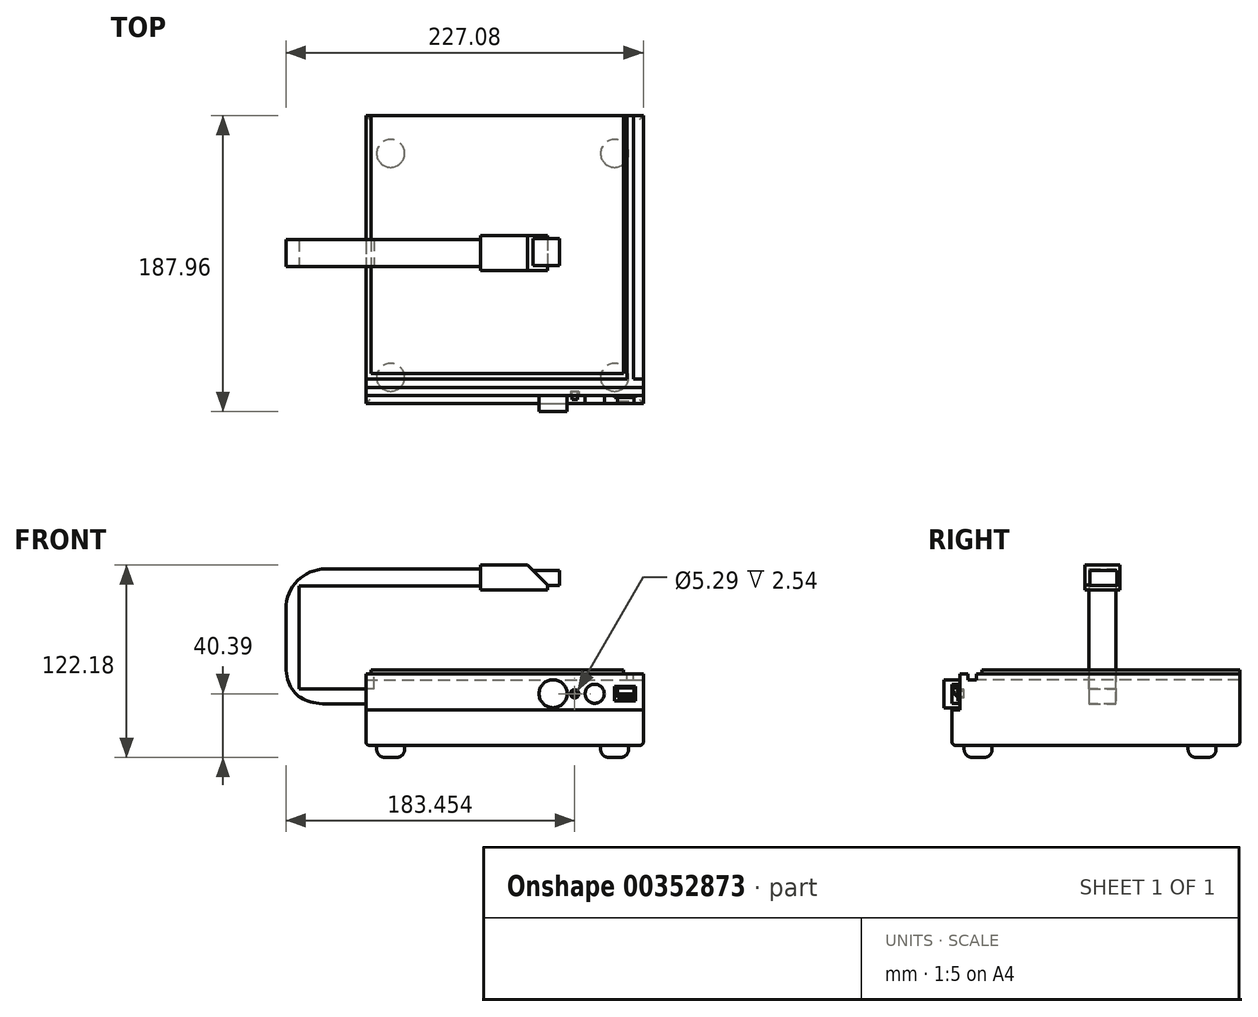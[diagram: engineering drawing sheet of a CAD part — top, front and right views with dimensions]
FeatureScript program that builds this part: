
annotation { "Feature Type Name" : "Feature", "Feature Type Description" : "" }
export const myFeature = defineFeature(function(context is Context, id is Id, definition is map)
    precondition{}
    {
        {
            var Q0;
            Q0=qCreatedBy(makeId("Front.planeOp"),FACE);
            var sketch = newSketch(context, id + "F0", { "sketchPlane" : qUnion([Q0])});
            skLineSegment(sketch, "E0.bottom", {"start": v(-86.87, 37.85) * mm, "end": v(89.4, 37.85) * mm});
            skLineSegment(sketch, "E0.top", {"start": v(-86.87, -32.77) * mm, "end": v(89.4, -32.77) * mm});
            skLineSegment(sketch, "E0.left", {"start": v(-86.87, 37.85) * mm, "end": v(-86.87, -32.77) * mm});
            skLineSegment(sketch, "E0.right", {"start": v(89.4, 37.85) * mm, "end": v(89.4, -32.77) * mm});
            skSolve(sketch);
        }
        {
            var Q0;
            Q0=makeQuery(id+"F0.imprint","IMPRINT",FACE,{"disambiguationData":[TD([[makeQuery(id+"F0.imprint","IMPRINT",EDGE,{"derivedFrom":sQuery(id+"F0.wireOp",EDGE,"E0.bottom")}),-1.0]])]});
            extrude(context, id + "F1", {"entities" : qUnion([Q0]), "depth" : 177.8 * mm});
        }
        {
            var Q0;
            Q0=makeQuery(id+"F1.opExtrude","SWEPT_FACE",FACE,{"disambiguationData":[OSD([sQuery(id+"F0.wireOp",EDGE,"E0.bottom")])]});
            extrude(context, id + "F2", {"entities" : qUnion([Q0]), "operationType" : NewBodyOperationType.REMOVE, "oppositeDirection" : true, "depth" : 25.4 * mm});
        }
        {
            var Q0;
            Q0=makeQuery(id+"F1.opExtrude","CAP_FACE",FACE,{"disambiguationData":[OSD([sQuery(id+"F0.wireOp",EDGE,"E0.bottom"),sQuery(id+"F0.wireOp",EDGE,"E0.top"),sQuery(id+"F0.wireOp",EDGE,"E0.left"),sQuery(id+"F0.wireOp",EDGE,"E0.right")])],"isStart":false});
            var sketch = newSketch(context, id + "F3", { "sketchPlane" : qUnion([Q0])});
            skLineSegment(sketch, "E1", {"start": v(-86.87, -10.16) * mm, "end": v(89.4, -10.16) * mm});
            skLineSegment(sketch, "E2", {"start": v(-86.87, -4.75) * mm, "end": v(89.4, -4.75) * mm});
            skSolve(sketch);
        }
        {
            var Q0;
            Q0 = qSketchRegion(id + "F3", true);
            var Q1;
            {var subQ0=sQuery(id+"F3.wireOp",EDGE,"E1");Q1=makeQuery(id+"F3.imprint","IMPRINT",FACE,{"disambiguationData":[TD([[makeQuery(id+"F3.imprint","IMPRINT",EDGE,{"derivedFrom":subQ0}),-1.0]])]});}
            extrude(context, id + "F4", {"entities" : qUnion([Q0, Q1]), "operationType" : NewBodyOperationType.ADD, "depth" : 5.08 * mm});
        }
        {
            var Q0;
            {var subQ0=sQuery(id+"F0.wireOp",EDGE,"E0.left");Q0=makeQuery(id+"F4.boolean.opBoolean","MERGE",FACE,{"derivedFrom":[makeQuery(id+"F1.opExtrude","SWEPT_FACE",FACE,{"disambiguationData":[OSD([subQ0])]}),makeQuery(id+"F4.opExtrude","SWEPT_FACE",FACE,{"disambiguationData":[OSD([subQ0])]})]});}
            var sketch = newSketch(context, id + "F5", { "sketchPlane" : qUnion([Q0])});
            skLineSegment(sketch, "E3.bottom", {"start": v(78.74, 12.45) * mm, "end": v(96.01, 12.45) * mm});
            skLineSegment(sketch, "E3.top", {"start": v(78.74, -6.35) * mm, "end": v(96.01, -6.35) * mm});
            skLineSegment(sketch, "E3.left", {"start": v(78.74, 12.45) * mm, "end": v(78.74, -6.35) * mm});
            skLineSegment(sketch, "E3.right", {"start": v(96.01, 12.45) * mm, "end": v(96.01, -6.35) * mm});
            skLineSegment(sketch, "E4", {"start": v(78.74, 3.05) * mm, "end": v(96.01, 3.05) * mm});
            skSolve(sketch);
        }
        {
            var Q0;
            {var subQ0=sQuery(id+"F5.wireOp",EDGE,"E3.top");Q0=makeQuery(id+"F5.imprint","IMPRINT",FACE,{"disambiguationData":[TD([[makeQuery(id+"F5.imprint","IMPRINT",EDGE,{"derivedFrom":subQ0}),1.0]])]});}
            extrude(context, id + "F6", {"entities" : qUnion([Q0]), "operationType" : NewBodyOperationType.ADD, "depth" : 50.8 * mm});
        }
        {
            var Q0;
            Q0=makeQuery(id+"F6.opExtrude","SWEPT_FACE",FACE,{"disambiguationData":[OSD([sQuery(id+"F5.wireOp",EDGE,"E4")])]});
            var sketch = newSketch(context, id + "F7", { "sketchPlane" : qUnion([Q0])});
            skLineSegment(sketch, "E5", {"start": v(-129.22, -96.01) * mm, "end": v(-129.22, -78.74) * mm});
            skSolve(sketch);
        }
        {
            var Q0;
            Q0 = qSketchRegion(id + "F7", true);
            var Q1;
            {var subQ0=sQuery(id+"F7.wireOp",EDGE,"E5");Q1=makeQuery(id+"F7.imprint","IMPRINT",FACE,{"disambiguationData":[TD([[makeQuery(id+"F7.imprint","IMPRINT",EDGE,{"derivedFrom":subQ0}),1.0]])]});}
            extrude(context, id + "F8", {"entities" : qUnion([Q0, Q1]), "operationType" : NewBodyOperationType.ADD, "depth" : 76.2 * mm});
        }
        {
            var Q0;
            Q0=makeQuery(id+"F8.opExtrude","SWEPT_FACE",FACE,{"disambiguationData":[OSD([sQuery(id+"F7.wireOp",EDGE,"E5")])]});
            var sketch = newSketch(context, id + "F9", { "sketchPlane" : qUnion([Q0])});
            skLineSegment(sketch, "E6", {"start": v(-78.74, 68.6) * mm, "end": v(-96.01, 68.6) * mm});
            skSolve(sketch);
        }
        {
            var Q0;
            Q0 = qSketchRegion(id + "F9", true);
            var Q1;
            {var subQ0=sQuery(id+"F9.wireOp",EDGE,"E6");Q1=makeQuery(id+"F9.imprint","IMPRINT",FACE,{"disambiguationData":[TD([[makeQuery(id+"F9.imprint","IMPRINT",EDGE,{"derivedFrom":subQ0}),-1.0]])]});}
            extrude(context, id + "F10", {"entities" : qUnion([Q0, Q1]), "operationType" : NewBodyOperationType.ADD, "depth" : 157.73 * mm});
        }
        {
            var Q0;
            Q0=makeQuery(id+"F10.opExtrude","CAP_EDGE",EDGE,{"disambiguationData":[OSD([sQuery(id+"F9.wireOp",EDGE,"E6")])],"isStart":true});
            var Q1;
            Q1=makeQuery(id+"F8.opExtrude","CAP_EDGE",EDGE,{"disambiguationData":[OSD([sQuery(id+"F5.wireOp",EDGE,"E4")])],"isStart":false});
            fillet(context, id + "F11", {"entities" : qUnion([Q0, Q1]), "radius" : 25.4 * mm, "tangentPropagation" : true, "allowEdgeOverflow" : false});
        }
        {
            var Q0;
            Q0=makeQuery(id+"F8.opExtrude","CAP_EDGE",EDGE,{"disambiguationData":[OSD([sQuery(id+"F7.wireOp",EDGE,"E5")])],"isStart":true});
            var Q1;
            Q1=makeQuery(id+"F6.opExtrude","CAP_EDGE",EDGE,{"disambiguationData":[OSD([sQuery(id+"F5.wireOp",EDGE,"E3.top")])],"isStart":false});
            fillet(context, id + "F12", {"entities" : qUnion([Q0, Q1]), "radius" : 25.4 * mm, "tangentPropagation" : true, "rho" : 0.5, "crossSection" : FilletCrossSection.CONIC, "allowEdgeOverflow" : false});
        }
        {
            var Q0;
            Q0=makeQuery(id+"F1.opExtrude","CAP_FACE",FACE,{"disambiguationData":[OSD([sQuery(id+"F0.wireOp",EDGE,"E0.bottom"),sQuery(id+"F0.wireOp",EDGE,"E0.top"),sQuery(id+"F0.wireOp",EDGE,"E0.left"),sQuery(id+"F0.wireOp",EDGE,"E0.right")])],"isStart":false});
            var sketch = newSketch(context, id + "F13", { "sketchPlane" : qUnion([Q0])});
            skCircle(sketch, "E7", {"center": v(58.46, 0) * mm, "radius": 6.08 * mm});
            skSolve(sketch);
        }
        {
            var Q0;
            Q0 = qSketchRegion(id + "F13", true);
            extrude(context, id + "F14", {"entities" : qUnion([Q0]), "operationType" : NewBodyOperationType.ADD, "depth" : 5.08 * mm});
        }
        {
            var Q0;
            Q0=makeQuery(id+"F1.opExtrude","CAP_FACE",FACE,{"disambiguationData":[OSD([sQuery(id+"F0.wireOp",EDGE,"E0.bottom"),sQuery(id+"F0.wireOp",EDGE,"E0.top"),sQuery(id+"F0.wireOp",EDGE,"E0.left"),sQuery(id+"F0.wireOp",EDGE,"E0.right")])],"isStart":false});
            var sketch = newSketch(context, id + "F15", { "sketchPlane" : qUnion([Q0])});
            skCircle(sketch, "E8", {"center": v(32.04, 0) * mm, "radius": 8.9 * mm});
            skSolve(sketch);
        }
        {
            var Q0;
            Q0 = qSketchRegion(id + "F15", true);
            extrude(context, id + "F16", {"entities" : qUnion([Q0]), "operationType" : NewBodyOperationType.ADD, "depth" : 10.16 * mm});
        }
        {
            var Q0;
            Q0=makeQuery(id+"F2.boolean.opBoolean","COPY",FACE,{"derivedFrom":makeQuery(id+"F2.opExtrude","CAP_FACE",FACE,{"disambiguationData":[OSD([sQuery(id+"F0.wireOp",EDGE,"E0.bottom")])],"isStart":false})});
            var sketch = newSketch(context, id + "F17", { "sketchPlane" : qUnion([Q0])});
            skLineSegment(sketch, "E9.bottom", {"start": v(-83.65, 0) * mm, "end": v(76.74, 0) * mm});
            skLineSegment(sketch, "E9.top", {"start": v(-83.65, -163.84) * mm, "end": v(76.74, -163.84) * mm});
            skLineSegment(sketch, "E9.left", {"start": v(-83.65, 0) * mm, "end": v(-83.65, -163.84) * mm});
            skLineSegment(sketch, "E9.right", {"start": v(76.74, 0) * mm, "end": v(76.74, -163.84) * mm});
            skSolve(sketch);
        }
        {
            var Q0;
            Q0 = qSketchRegion(id + "F17", true);
            extrude(context, id + "F18", {"entities" : qUnion([Q0]), "operationType" : NewBodyOperationType.ADD, "depth" : 2.54 * mm});
        }
        {
            var Q0;
            {var subQ0=sQuery(id+"F0.wireOp",EDGE,"E0.left");Q0=makeQuery(id+"F4.boolean.opBoolean","MERGE",FACE,{"derivedFrom":[makeQuery(id+"F1.opExtrude","SWEPT_FACE",FACE,{"disambiguationData":[OSD([subQ0])]}),makeQuery(id+"F4.opExtrude","SWEPT_FACE",FACE,{"disambiguationData":[OSD([subQ0])]})]});}
            var sketch = newSketch(context, id + "F19", { "sketchPlane" : qUnion([Q0])});
            skLineSegment(sketch, "E10.bottom", {"start": v(96.01, 3.05) * mm, "end": v(78.68, 3.05) * mm});
            skLineSegment(sketch, "E10.top", {"start": v(96.01, 12.45) * mm, "end": v(78.68, 12.45) * mm});
            skLineSegment(sketch, "E10.left", {"start": v(96.01, 3.05) * mm, "end": v(96.01, 12.45) * mm});
            skLineSegment(sketch, "E10.right", {"start": v(78.68, 3.05) * mm, "end": v(78.68, 12.45) * mm});
            skSolve(sketch);
        }
        {
            var Q0;
            Q0 = qSketchRegion(id + "F19", true);
            extrude(context, id + "F20", {"entities" : qUnion([Q0]), "operationType" : NewBodyOperationType.REMOVE, "oppositeDirection" : true, "depth" : 5.08 * mm});
        }
        {
            var Q0;
            {var subQ1=sQuery(id+"F0.wireOp",EDGE,"E0.right");var subQ3=sQuery(id+"F0.wireOp",EDGE,"E0.bottom");Q0=makeQuery(id+"F20.boolean.opBoolean","SPLIT",FACE,{"disambiguationData":[TD([makeQuery(id+"F1.opExtrude","SWEPT_FACE",FACE,{"disambiguationData":[OSD([subQ1])]})])],"derivedFrom":makeQuery(id+"F2.boolean.opBoolean","COPY",FACE,{"derivedFrom":makeQuery(id+"F2.opExtrude","CAP_FACE",FACE,{"disambiguationData":[OSD([subQ3])],"isStart":false})})});}
            var sketch = newSketch(context, id + "F21", { "sketchPlane" : qUnion([Q0])});
            skLineSegment(sketch, "E11.bottom", {"start": v(-86.87, -167.28) * mm, "end": v(89.4, -167.28) * mm});
            skLineSegment(sketch, "E11.top", {"start": v(-86.87, -172.6) * mm, "end": v(89.4, -172.6) * mm});
            skLineSegment(sketch, "E11.left", {"start": v(-86.87, -167.28) * mm, "end": v(-86.87, -172.6) * mm});
            skLineSegment(sketch, "E11.right", {"start": v(89.4, -167.28) * mm, "end": v(89.4, -172.6) * mm});
            skPoint(sketch, "E12.oppositeSnap0", {"position": v(83.07, 0) * mm});
            skLineSegment(sketch, "E12.bottom", {"start": v(78.93, 0) * mm, "end": v(83.07, 0) * mm});
            skLineSegment(sketch, "E12.top", {"start": v(78.93, -167.28) * mm, "end": v(83.07, -167.28) * mm});
            skLineSegment(sketch, "E12.left", {"start": v(78.93, 0) * mm, "end": v(78.93, -167.28) * mm});
            skLineSegment(sketch, "E12.right", {"start": v(83.07, 0) * mm, "end": v(83.07, -167.28) * mm});
            skSolve(sketch);
        }
        {
            var Q0;
            Q0 = qSketchRegion(id + "F21", true);
            extrude(context, id + "F22", {"entities" : qUnion([Q0]), "operationType" : NewBodyOperationType.REMOVE, "oppositeDirection" : true, "depth" : 3.8 * mm});
        }
        {
            var Q0;
            Q0=makeQuery(id+"F1.opExtrude","CAP_FACE",FACE,{"disambiguationData":[OSD([sQuery(id+"F0.wireOp",EDGE,"E0.bottom"),sQuery(id+"F0.wireOp",EDGE,"E0.top"),sQuery(id+"F0.wireOp",EDGE,"E0.left"),sQuery(id+"F0.wireOp",EDGE,"E0.right")])],"isStart":false});
            var sketch = newSketch(context, id + "F23", { "sketchPlane" : qUnion([Q0])});
            skLineSegment(sketch, "E13.bottom", {"start": v(71.1, 4.67) * mm, "end": v(84.47, 4.67) * mm});
            skLineSegment(sketch, "E13.top", {"start": v(71.1, -4.5) * mm, "end": v(84.47, -4.5) * mm});
            skLineSegment(sketch, "E13.left", {"start": v(71.1, 4.67) * mm, "end": v(71.1, -4.5) * mm});
            skLineSegment(sketch, "E13.right", {"start": v(84.47, 4.67) * mm, "end": v(84.47, -4.5) * mm});
            skSolve(sketch);
        }
        {
            var Q0;
            Q0 = qSketchRegion(id + "F23", true);
            extrude(context, id + "F24", {"entities" : qUnion([Q0]), "operationType" : NewBodyOperationType.ADD, "depth" : 1.27 * mm});
        }
        {
            var Q0;
            {var subQ0=sQuery(id+"F0.wireOp",EDGE,"E0.top");Q0=makeQuery(id+"F4.boolean.opBoolean","MERGE",FACE,{"derivedFrom":[makeQuery(id+"F1.opExtrude","SWEPT_FACE",FACE,{"disambiguationData":[OSD([subQ0])]}),makeQuery(id+"F4.opExtrude","SWEPT_FACE",FACE,{"disambiguationData":[OSD([subQ0])]})]});}
            fillet(context, id + "F25", {"entities" : qUnion([Q0]), "radius" : 2.54 * mm, "tangentPropagation" : true, "rho" : 0.5, "crossSection" : FilletCrossSection.CONIC, "allowEdgeOverflow" : false});
        }
        {
            var Q0;
            Q0=makeQuery(id+"F24.opExtrude","CAP_FACE",FACE,{"disambiguationData":[OSD([sQuery(id+"F23.wireOp",EDGE,"E13.bottom"),sQuery(id+"F23.wireOp",EDGE,"E13.top"),sQuery(id+"F23.wireOp",EDGE,"E13.left"),sQuery(id+"F23.wireOp",EDGE,"E13.right")])],"isStart":false});
            var sketch = newSketch(context, id + "F26", { "sketchPlane" : qUnion([Q0])});
            skLineSegment(sketch, "E14.bottom", {"start": v(83.37, 3.58) * mm, "end": v(72.82, 3.58) * mm});
            skLineSegment(sketch, "E14.top", {"start": v(83.37, -3.58) * mm, "end": v(72.82, -3.58) * mm});
            skLineSegment(sketch, "E14.left", {"start": v(83.37, 3.58) * mm, "end": v(83.37, -3.58) * mm});
            skLineSegment(sketch, "E14.right", {"start": v(72.82, 3.58) * mm, "end": v(72.82, -3.58) * mm});
            skPoint(sketch, "E14.middle", {"position": v(78.1, 0) * mm});
            skSolve(sketch);
        }
        {
            var Q0;
            Q0=makeQuery(id+"F26.imprint","IMPRINT",FACE,{"disambiguationData":[TD([[makeQuery(id+"F26.imprint","IMPRINT",EDGE,{"derivedFrom":sQuery(id+"F26.wireOp",EDGE,"E14.bottom")}),1.0]])]});
            extrude(context, id + "F27", {"entities" : qUnion([Q0]), "operationType" : NewBodyOperationType.ADD, "depth" : 3.8 * mm});
        }
        {
            var Q0;
            Q0=makeQuery(id+"F27.opExtrude","CAP_EDGE",EDGE,{"disambiguationData":[OSD([sQuery(id+"F26.wireOp",EDGE,"E14.top")])],"isStart":false});
            chamfer(context, id + "F28", {"entities" : qUnion([Q0]), "width" : 5.08 * mm, "tangentPropagation" : true});
        }
        {
            var Q0;
            {var subQ0=sQuery(id+"F26.wireOp",EDGE,"E14.top");Q0=makeQuery(id+"F28.opChamfer","BLEND_EDGE",EDGE,{"blendedFrom":[makeQuery(id+"F27.opExtrude","CAP_EDGE",EDGE,{"disambiguationData":[OSD([subQ0])],"isStart":false}),makeQuery(id+"F27.opExtrude","CAP_FACE",FACE,{"disambiguationData":[OSD([sQuery(id+"F26.wireOp",EDGE,"E14.bottom"),subQ0,sQuery(id+"F26.wireOp",EDGE,"E14.left"),sQuery(id+"F26.wireOp",EDGE,"E14.right")])],"isStart":false})],"blendedInto":[makeQuery(id+"F27.opExtrude","CAP_FACE",FACE,{"disambiguationData":[OSD([sQuery(id+"F26.wireOp",EDGE,"E14.bottom"),subQ0,sQuery(id+"F26.wireOp",EDGE,"E14.left"),sQuery(id+"F26.wireOp",EDGE,"E14.right")])],"isStart":false})]});}
            chamfer(context, id + "F29", {"entities" : qUnion([Q0]), "width" : 5.08 * mm, "tangentPropagation" : true});
        }
        {
            var Q0;
            Q0=makeQuery(id+"F1.opExtrude","CAP_FACE",FACE,{"disambiguationData":[OSD([sQuery(id+"F0.wireOp",EDGE,"E0.bottom"),sQuery(id+"F0.wireOp",EDGE,"E0.top"),sQuery(id+"F0.wireOp",EDGE,"E0.left"),sQuery(id+"F0.wireOp",EDGE,"E0.right")])],"isStart":false});
            var sketch = newSketch(context, id + "F30", { "sketchPlane" : qUnion([Q0])});
            skCircle(sketch, "E15", {"center": v(45.78, 0) * mm, "radius": 2.64 * mm});
            skSolve(sketch);
        }
        {
            var Q0;
            Q0=makeQuery(id+"F30.imprint","IMPRINT",FACE,{"disambiguationData":[TD([[makeQuery(id+"F30.imprint","IMPRINT",EDGE,{"derivedFrom":sQuery(id+"F30.wireOp",EDGE,"E15")}),1.0]])]});
            extrude(context, id + "F31", {"entities" : qUnion([Q0]), "operationType" : NewBodyOperationType.REMOVE, "oppositeDirection" : true, "depth" : 2.54 * mm});
        }
        {
            var Q0;
            Q0=makeQuery(id+"F31.boolean.opBoolean","COPY",FACE,{"derivedFrom":makeQuery(id+"F31.opExtrude","CAP_FACE",FACE,{"disambiguationData":[OSD([sQuery(id+"F30.wireOp",EDGE,"E15")])],"isStart":false})});
            var sketch = newSketch(context, id + "F32", { "sketchPlane" : qUnion([Q0])});
            skCircle(sketch, "E16", {"center": v(45.78, 0) * mm, "radius": 1.76 * mm});
            skSolve(sketch);
        }
        {
            var Q0;
            Q0 = qSketchRegion(id + "F32", true);
            extrude(context, id + "F33", {"entities" : qUnion([Q0]), "operationType" : NewBodyOperationType.ADD, "depth" : 5.08 * mm});
        }
        {
            var Q0;
            {var subQ0=sQuery(id+"F0.wireOp",EDGE,"E0.top");Q0=makeQuery(id+"F4.boolean.opBoolean","MERGE",FACE,{"derivedFrom":[makeQuery(id+"F1.opExtrude","SWEPT_FACE",FACE,{"disambiguationData":[OSD([subQ0])]}),makeQuery(id+"F4.opExtrude","SWEPT_FACE",FACE,{"disambiguationData":[OSD([subQ0])]})]});}
            var sketch = newSketch(context, id + "F34", { "sketchPlane" : qUnion([Q0])});
            skLineSegment(sketch, "E17.bottom", {"start": v(71.12, 166.26) * mm, "end": v(-71.12, 166.26) * mm});
            skLineSegment(sketch, "E17.top", {"start": v(71.12, 24.02) * mm, "end": v(-71.12, 24.02) * mm});
            skLineSegment(sketch, "E17.left", {"start": v(71.12, 166.26) * mm, "end": v(71.12, 24.02) * mm});
            skLineSegment(sketch, "E17.right", {"start": v(-71.12, 166.26) * mm, "end": v(-71.12, 24.02) * mm});
            skPoint(sketch, "E17.middle", {"position": v(0, 95.14) * mm});
            skCircle(sketch, "E18", {"center": v(-71.12, 166.26) * mm, "radius": 8.9 * mm});
            skCircle(sketch, "E19", {"center": v(71.12, 166.26) * mm, "radius": 8.9 * mm});
            skCircle(sketch, "E20", {"center": v(71.12, 24.02) * mm, "radius": 8.9 * mm});
            skCircle(sketch, "E21", {"center": v(-71.12, 24.02) * mm, "radius": 8.9 * mm});
            skSolve(sketch);
        }
        {
            var Q0;
            {var subQ0=sQuery(id+"F34.wireOp",EDGE,"E17.right");var subQ1=sQuery(id+"F34.wireOp",EDGE,"E17.bottom");var subQ2=makeQuery(id+"F34.imprint","INTERSECT",VERTEX,{"derivedFrom":[subQ1,subQ0]});Q0=makeQuery(id+"F34.imprint","IMPRINT",FACE,{"disambiguationData":[TD([[makeQuery(id+"F34.imprint","IMPRINT",EDGE,{"disambiguationData":[TD([[subQ2,1.0]])],"derivedFrom":subQ1}),1.0]])]});}
            var Q1;
            {var subQ0=sQuery(id+"F34.wireOp",EDGE,"E17.right");var subQ1=sQuery(id+"F34.wireOp",EDGE,"E17.bottom");var subQ2=makeQuery(id+"F34.imprint","INTERSECT",VERTEX,{"derivedFrom":[subQ1,subQ0]});Q1=makeQuery(id+"F34.imprint","IMPRINT",FACE,{"disambiguationData":[TD([[makeQuery(id+"F34.imprint","IMPRINT",EDGE,{"disambiguationData":[TD([[subQ2,1.0]])],"derivedFrom":subQ1}),-1.0]])]});}
            var Q2;
            {var subQ0=sQuery(id+"F34.wireOp",EDGE,"E17.left");var subQ1=sQuery(id+"F34.wireOp",EDGE,"E17.bottom");var subQ2=makeQuery(id+"F34.imprint","INTERSECT",VERTEX,{"derivedFrom":[subQ1,subQ0]});Q2=makeQuery(id+"F34.imprint","IMPRINT",FACE,{"disambiguationData":[TD([[makeQuery(id+"F34.imprint","IMPRINT",EDGE,{"disambiguationData":[TD([[subQ2,-1.0]])],"derivedFrom":subQ1}),-1.0]])]});}
            var Q3;
            {var subQ0=sQuery(id+"F34.wireOp",EDGE,"E17.left");var subQ1=sQuery(id+"F34.wireOp",EDGE,"E17.bottom");var subQ2=makeQuery(id+"F34.imprint","INTERSECT",VERTEX,{"derivedFrom":[subQ1,subQ0]});Q3=makeQuery(id+"F34.imprint","IMPRINT",FACE,{"disambiguationData":[TD([[makeQuery(id+"F34.imprint","IMPRINT",EDGE,{"disambiguationData":[TD([[subQ2,-1.0]])],"derivedFrom":subQ1}),1.0]])]});}
            var Q4;
            {var subQ0=sQuery(id+"F34.wireOp",EDGE,"E17.left");var subQ1=sQuery(id+"F34.wireOp",EDGE,"E17.top");var subQ2=makeQuery(id+"F34.imprint","INTERSECT",VERTEX,{"derivedFrom":[subQ1,subQ0]});Q4=makeQuery(id+"F34.imprint","IMPRINT",FACE,{"disambiguationData":[TD([[makeQuery(id+"F34.imprint","IMPRINT",EDGE,{"disambiguationData":[TD([[subQ2,-1.0]])],"derivedFrom":subQ1}),-1.0]])]});}
            var Q5;
            {var subQ0=sQuery(id+"F34.wireOp",EDGE,"E17.left");var subQ1=sQuery(id+"F34.wireOp",EDGE,"E17.top");var subQ2=makeQuery(id+"F34.imprint","INTERSECT",VERTEX,{"derivedFrom":[subQ1,subQ0]});Q5=makeQuery(id+"F34.imprint","IMPRINT",FACE,{"disambiguationData":[TD([[makeQuery(id+"F34.imprint","IMPRINT",EDGE,{"disambiguationData":[TD([[subQ2,-1.0]])],"derivedFrom":subQ1}),1.0]])]});}
            var Q6;
            {var subQ0=sQuery(id+"F34.wireOp",EDGE,"E17.right");var subQ1=sQuery(id+"F34.wireOp",EDGE,"E17.top");var subQ2=makeQuery(id+"F34.imprint","INTERSECT",VERTEX,{"derivedFrom":[subQ1,subQ0]});Q6=makeQuery(id+"F34.imprint","IMPRINT",FACE,{"disambiguationData":[TD([[makeQuery(id+"F34.imprint","IMPRINT",EDGE,{"disambiguationData":[TD([[subQ2,1.0]])],"derivedFrom":subQ1}),1.0]])]});}
            var Q7;
            {var subQ0=sQuery(id+"F34.wireOp",EDGE,"E17.right");var subQ1=sQuery(id+"F34.wireOp",EDGE,"E17.top");var subQ2=makeQuery(id+"F34.imprint","INTERSECT",VERTEX,{"derivedFrom":[subQ1,subQ0]});Q7=makeQuery(id+"F34.imprint","IMPRINT",FACE,{"disambiguationData":[TD([[makeQuery(id+"F34.imprint","IMPRINT",EDGE,{"disambiguationData":[TD([[subQ2,1.0]])],"derivedFrom":subQ1}),-1.0]])]});}
            extrude(context, id + "F35", {"entities" : qUnion([Q0, Q1, Q2, Q3, Q4, Q5, Q6, Q7]), "operationType" : NewBodyOperationType.ADD, "depth" : 7.62 * mm});
        }
        {
            var Q0;
            Q0=makeQuery(id+"F35.opExtrude","CAP_EDGE",EDGE,{"disambiguationData":[OSD([sQuery(id+"F34.wireOp",EDGE,"E18")])],"isStart":false});
            var Q1;
            Q1=makeQuery(id+"F35.opExtrude","CAP_EDGE",EDGE,{"disambiguationData":[OSD([sQuery(id+"F34.wireOp",EDGE,"E19")])],"isStart":false});
            var Q2;
            Q2=makeQuery(id+"F35.opExtrude","CAP_EDGE",EDGE,{"disambiguationData":[OSD([sQuery(id+"F34.wireOp",EDGE,"E20")])],"isStart":false});
            var Q3;
            Q3=makeQuery(id+"F35.opExtrude","CAP_EDGE",EDGE,{"disambiguationData":[OSD([sQuery(id+"F34.wireOp",EDGE,"E21")])],"isStart":false});
            fillet(context, id + "F36", {"entities" : qUnion([Q0, Q1, Q2, Q3]), "radius" : 5.08 * mm, "tangentPropagation" : true, "allowEdgeOverflow" : false});
        }
        {
            var Q0;
            {var subQ0=sQuery(id+"F5.wireOp",EDGE,"E4");var subQ1=sQuery(id+"F5.wireOp",EDGE,"E3.right");Q0=makeQuery(id+"F10.boolean.opBoolean","MERGE",FACE,{"derivedFrom":[makeQuery(id+"F8.boolean.opBoolean","MERGE",FACE,{"derivedFrom":[makeQuery(id+"F6.opExtrude","SWEPT_FACE",FACE,{"disambiguationData":[OSD([subQ1])]}),makeQuery(id+"F8.opExtrude","SWEPT_FACE",FACE,{"disambiguationData":[OSD([subQ1,subQ0])]})]}),makeQuery(id+"F10.opExtrude","SWEPT_FACE",FACE,{"disambiguationData":[OSD([subQ1,subQ0,sQuery(id+"F7.wireOp",EDGE,"E5")])]})]});}
            var sketch = newSketch(context, id + "F37", { "sketchPlane" : qUnion([Q0])});
            skLineSegment(sketch, "E22", {"start": v(11.28, 79.25) * mm, "end": v(11.28, 68.6) * mm});
            skPoint(sketch, "E23.endSnap0", {"position": v(11.28, 73.92) * mm});
            skSolve(sketch);
        }
        {
            var Q0;
            {var subQ0=sQuery(id+"F37.wireOp",EDGE,"E22");Q0=makeQuery(id+"F37.imprint","IMPRINT",FACE,{"disambiguationData":[TD([[makeQuery(id+"F37.imprint","IMPRINT",EDGE,{"derivedFrom":subQ0}),1.0]])]});}
            extrude(context, id + "F38", {"entities" : qUnion([Q0]), "operationType" : NewBodyOperationType.ADD, "depth" : 2.54 * mm});
        }
        {
            var Q0;
            {var subQ0=sQuery(id+"F7.wireOp",EDGE,"E5");var subQ1=sQuery(id+"F5.wireOp",EDGE,"E4");var subQ2=sQuery(id+"F5.wireOp",EDGE,"E3.right");var subQ3=makeQuery(id+"F10.boolean.opBoolean","MERGE",EDGE,{"derivedFrom":[makeQuery(id+"F8.opExtrude","CAP_EDGE",EDGE,{"disambiguationData":[OSD([subQ2,subQ1])],"isStart":false}),makeQuery(id+"F10.opExtrude","SWEPT_EDGE",EDGE,{"disambiguationData":[OSD([subQ2,subQ1,subQ0])]})]});Q0=makeQuery(id+"F38.boolean.opBoolean","MERGE",FACE,{"derivedFrom":[makeQuery(id+"F10.boolean.opBoolean","MERGE",FACE,{"derivedFrom":[makeQuery(id+"F8.opExtrude","CAP_FACE",FACE,{"disambiguationData":[OSD([sQuery(id+"F5.wireOp",EDGE,"E3.left"),subQ2,subQ1,subQ0])],"isStart":false}),makeQuery(id+"F10.opExtrude","SWEPT_FACE",FACE,{"disambiguationData":[OSD([subQ0])]})]}),makeQuery(id+"F38.opExtrude","SWEPT_FACE",FACE,{"disambiguationData":[OSD([subQ2,subQ1,subQ0]),TDD([makeQuery(id+"F37.imprint","IMPRINT",EDGE,{"disambiguationData":[TD([[makeQuery(id+"F37.imprint","INTERSECT",VERTEX,{"derivedFrom":[subQ3,sQuery(id+"F37.wireOp",EDGE,"E22")]}),-1.0]])],"derivedFrom":subQ3})])]})]});}
            var sketch = newSketch(context, id + "F39", { "sketchPlane" : qUnion([Q0])});
            skLineSegment(sketch, "E24", {"start": v(11.28, -96.01) * mm, "end": v(28.52, -96.01) * mm});
            skLineSegment(sketch, "E25", {"start": v(11.28, -96.01) * mm, "end": v(11.28, -78.74) * mm});
            skSolve(sketch);
        }
        {
            var Q0;
            {var subQ0=sQuery(id+"F39.wireOp",EDGE,"E24");Q0=makeQuery(id+"F39.imprint","IMPRINT",FACE,{"disambiguationData":[TD([[makeQuery(id+"F39.imprint","IMPRINT",EDGE,{"derivedFrom":subQ0}),1.0]])]});}
            var Q1;
            {var subQ0=sQuery(id+"F39.wireOp",EDGE,"E24");Q1=makeQuery(id+"F39.imprint","IMPRINT",FACE,{"disambiguationData":[TD([[makeQuery(id+"F39.imprint","IMPRINT",EDGE,{"derivedFrom":subQ0}),-1.0]])]});}
            extrude(context, id + "F40", {"entities" : qUnion([Q0, Q1]), "operationType" : NewBodyOperationType.ADD, "depth" : 2.54 * mm});
        }
        {
            var Q0;
            {var subQ0=sQuery(id+"F7.wireOp",EDGE,"E5");var subQ1=sQuery(id+"F5.wireOp",EDGE,"E4");var subQ2=sQuery(id+"F5.wireOp",EDGE,"E3.left");Q0=makeQuery(id+"F40.boolean.opBoolean","MERGE",FACE,{"derivedFrom":[makeQuery(id+"F10.boolean.opBoolean","MERGE",FACE,{"derivedFrom":[makeQuery(id+"F8.boolean.opBoolean","MERGE",FACE,{"derivedFrom":[makeQuery(id+"F6.opExtrude","SWEPT_FACE",FACE,{"disambiguationData":[OSD([subQ2])]}),makeQuery(id+"F8.opExtrude","SWEPT_FACE",FACE,{"disambiguationData":[OSD([subQ2,subQ1])]})]}),makeQuery(id+"F10.opExtrude","SWEPT_FACE",FACE,{"disambiguationData":[OSD([subQ2,subQ1,subQ0])]})]}),makeQuery(id+"F40.opExtrude","SWEPT_FACE",FACE,{"disambiguationData":[OSD([subQ2,subQ1,subQ0])]})]});}
            var sketch = newSketch(context, id + "F41", { "sketchPlane" : qUnion([Q0])});
            skLineSegment(sketch, "E26", {"start": v(-11.28, 79.25) * mm, "end": v(-28.52, 79.25) * mm});
            skLineSegment(sketch, "E27", {"start": v(-11.28, 79.25) * mm, "end": v(-11.28, 68.6) * mm});
            skSolve(sketch);
        }
        {
            var Q0;
            {var subQ0=sQuery(id+"F41.wireOp",EDGE,"E26");Q0=makeQuery(id+"F41.imprint","IMPRINT",FACE,{"disambiguationData":[TD([[makeQuery(id+"F41.imprint","IMPRINT",EDGE,{"derivedFrom":subQ0}),-1.0]])]});}
            var Q1;
            {var subQ0=sQuery(id+"F41.wireOp",EDGE,"E26");Q1=makeQuery(id+"F41.imprint","IMPRINT",FACE,{"disambiguationData":[TD([[makeQuery(id+"F41.imprint","IMPRINT",EDGE,{"derivedFrom":subQ0}),1.0]])]});}
            extrude(context, id + "F42", {"entities" : qUnion([Q0, Q1]), "operationType" : NewBodyOperationType.ADD, "depth" : 2.54 * mm});
        }
        {
            var Q0;
            {var subQ0=sQuery(id+"F9.wireOp",EDGE,"E6");var subQ1=sQuery(id+"F7.wireOp",EDGE,"E5");var subQ2=sQuery(id+"F5.wireOp",EDGE,"E4");Q0=makeQuery(id+"F42.boolean.opBoolean","MERGE",FACE,{"derivedFrom":[makeQuery(id+"F38.boolean.opBoolean","MERGE",FACE,{"derivedFrom":[makeQuery(id+"F10.opExtrude","SWEPT_FACE",FACE,{"disambiguationData":[OSD([subQ0])]}),makeQuery(id+"F38.opExtrude","SWEPT_FACE",FACE,{"disambiguationData":[OSD([sQuery(id+"F5.wireOp",EDGE,"E3.right"),subQ2,subQ1,subQ0])]})]}),makeQuery(id+"F42.opExtrude","SWEPT_FACE",FACE,{"disambiguationData":[OSD([sQuery(id+"F5.wireOp",EDGE,"E3.left"),subQ2,subQ1,subQ0])]})]});}
            var sketch = newSketch(context, id + "F43", { "sketchPlane" : qUnion([Q0])});
            skLineSegment(sketch, "E28", {"start": v(11.28, 96.01) * mm, "end": v(11.28, 78.74) * mm});
            skSolve(sketch);
        }
        {
            var Q0;
            Q0=makeQuery(id+"F43.imprint","IMPRINT",FACE,{"disambiguationData":[TD([[makeQuery(id+"F43.imprint","IMPRINT",EDGE,{"derivedFrom":sQuery(id+"F43.wireOp",EDGE,"E28")}),1.0]])]});
            extrude(context, id + "F44", {"entities" : qUnion([Q0]), "operationType" : NewBodyOperationType.ADD, "depth" : 2.54 * mm});
        }
        {
            var Q0;
            {var subQ0=sQuery(id+"F9.wireOp",EDGE,"E6");var subQ1=sQuery(id+"F7.wireOp",EDGE,"E5");var subQ2=sQuery(id+"F5.wireOp",EDGE,"E4");var subQ3=sQuery(id+"F5.wireOp",EDGE,"E3.right");var subQ4=sQuery(id+"F5.wireOp",EDGE,"E3.left");var subQ5=makeQuery(id+"F38.boolean.opBoolean","MERGE",EDGE,{"derivedFrom":[makeQuery(id+"F10.opExtrude","CAP_EDGE",EDGE,{"disambiguationData":[OSD([subQ1])],"isStart":false}),makeQuery(id+"F38.opExtrude","SWEPT_EDGE",EDGE,{"disambiguationData":[OSD([subQ3,subQ2,subQ1])]})]});var subQ7=makeQuery(id+"F10.opExtrude","CAP_EDGE",EDGE,{"disambiguationData":[OSD([subQ3,subQ2,subQ1])],"isStart":false});var subQ8=makeQuery(id+"F39.imprint","INTERSECT",VERTEX,{"derivedFrom":[subQ5,sQuery(id+"F39.wireOp",EDGE,"E24")]});Q0=makeQuery(id+"F44.boolean.opBoolean","MERGE",FACE,{"derivedFrom":[makeQuery(id+"F42.boolean.opBoolean","MERGE",FACE,{"derivedFrom":[makeQuery(id+"F40.boolean.opBoolean","MERGE",FACE,{"derivedFrom":[makeQuery(id+"F38.boolean.opBoolean","MERGE",FACE,{"derivedFrom":[makeQuery(id+"F10.opExtrude","CAP_FACE",FACE,{"disambiguationData":[OSD([subQ4,subQ3,subQ2,subQ1,subQ0])],"isStart":false}),makeQuery(id+"F38.opExtrude","SWEPT_FACE",FACE,{"disambiguationData":[OSD([subQ3,subQ2,subQ1]),TDD([makeQuery(id+"F37.imprint","IMPRINT",EDGE,{"derivedFrom":subQ7})])]})]}),makeQuery(id+"F40.opExtrude","SWEPT_FACE",FACE,{"disambiguationData":[OSD([subQ3,subQ2,subQ1]),TDD([makeQuery(id+"F39.imprint","IMPRINT",EDGE,{"disambiguationData":[TD([[subQ8,-1.0]])],"derivedFrom":subQ5}),makeQuery(id+"F39.imprint","IMPRINT",EDGE,{"disambiguationData":[TD([[subQ8,1.0]])],"derivedFrom":subQ5})])]})]}),makeQuery(id+"F42.opExtrude","SWEPT_FACE",FACE,{"disambiguationData":[OSD([subQ4,subQ3,subQ2,subQ1])]})]}),makeQuery(id+"F44.opExtrude","SWEPT_FACE",FACE,{"disambiguationData":[OSD([subQ4,subQ3,subQ2,subQ1,subQ0])]})]});}
            var sketch = newSketch(context, id + "F45", { "sketchPlane" : qUnion([Q0])});
            skLineSegment(sketch, "E29.bottom", {"start": v(-78.24, 78.29) * mm, "end": v(-95.4, 78.29) * mm});
            skLineSegment(sketch, "E29.top", {"start": v(-78.24, 68.65) * mm, "end": v(-95.4, 68.65) * mm});
            skLineSegment(sketch, "E29.left", {"start": v(-78.24, 78.29) * mm, "end": v(-78.24, 68.65) * mm});
            skLineSegment(sketch, "E29.right", {"start": v(-95.4, 78.29) * mm, "end": v(-95.4, 68.65) * mm});
            skPoint(sketch, "E29.middle", {"position": v(-86.82, 73.47) * mm});
            skSolve(sketch);
        }
        {
            var Q0;
            Q0 = qSketchRegion(id + "F45", true);
            extrude(context, id + "F46", {"entities" : qUnion([Q0]), "operationType" : NewBodyOperationType.ADD, "depth" : 7.62 * mm});
        }
        {
            var Q0;
            {var subQ0=sQuery(id+"F7.wireOp",EDGE,"E5");var subQ1=sQuery(id+"F5.wireOp",EDGE,"E4");var subQ2=sQuery(id+"F5.wireOp",EDGE,"E3.right");var subQ3=sQuery(id+"F5.wireOp",EDGE,"E3.left");var subQ4=makeQuery(id+"F38.boolean.opBoolean","MERGE",EDGE,{"derivedFrom":[makeQuery(id+"F10.opExtrude","CAP_EDGE",EDGE,{"disambiguationData":[OSD([subQ0])],"isStart":false}),makeQuery(id+"F38.opExtrude","SWEPT_EDGE",EDGE,{"disambiguationData":[OSD([subQ2,subQ1,subQ0])]})]});var subQ6=makeQuery(id+"F39.imprint","INTERSECT",VERTEX,{"derivedFrom":[subQ4,sQuery(id+"F39.wireOp",EDGE,"E24")]});Q0=makeQuery(id+"F42.boolean.opBoolean","MERGE",EDGE,{"derivedFrom":[makeQuery(id+"F40.opExtrude","CAP_EDGE",EDGE,{"disambiguationData":[OSD([subQ2,subQ1,subQ0]),TDD([makeQuery(id+"F39.imprint","IMPRINT",EDGE,{"disambiguationData":[TD([[subQ6,-1.0]])],"derivedFrom":subQ4}),makeQuery(id+"F39.imprint","IMPRINT",EDGE,{"disambiguationData":[TD([[subQ6,1.0]])],"derivedFrom":subQ4})])],"isStart":false}),makeQuery(id+"F42.opExtrude","SWEPT_EDGE",EDGE,{"disambiguationData":[OSD([subQ3,subQ2,subQ1,subQ0])]})]});}
            chamfer(context, id + "F47", {"entities" : qUnion([Q0]), "width" : 12.7 * mm, "tangentPropagation" : true});
        }
        {
            var Q0;
            {var subQ0=sQuery(id+"F41.wireOp",EDGE,"E27");var subQ1=sQuery(id+"F37.wireOp",EDGE,"E22");var subQ2=sQuery(id+"F7.wireOp",EDGE,"E5");var subQ3=sQuery(id+"F5.wireOp",EDGE,"E4");var subQ4=sQuery(id+"F5.wireOp",EDGE,"E3.right");var subQ5=sQuery(id+"F5.wireOp",EDGE,"E3.left");var subQ6=sQuery(id+"F39.wireOp",EDGE,"E25");Q0=makeQuery(id+"F44.boolean.opBoolean","MERGE",FACE,{"derivedFrom":[makeQuery(id+"F42.boolean.opBoolean","MERGE",FACE,{"derivedFrom":[makeQuery(id+"F40.boolean.opBoolean","MERGE",FACE,{"derivedFrom":[makeQuery(id+"F38.opExtrude","SWEPT_FACE",FACE,{"disambiguationData":[OSD([subQ1])]}),makeQuery(id+"F40.opExtrude","SWEPT_FACE",FACE,{"disambiguationData":[OSD([subQ4,subQ3,subQ2,subQ1,subQ6])]})]}),makeQuery(id+"F42.opExtrude","SWEPT_FACE",FACE,{"disambiguationData":[OSD([subQ5,subQ3,subQ2,subQ6,subQ0])]})]}),makeQuery(id+"F44.opExtrude","SWEPT_FACE",FACE,{"disambiguationData":[OSD([subQ5,subQ4,subQ3,subQ2,sQuery(id+"F9.wireOp",EDGE,"E6"),subQ1,subQ0,sQuery(id+"F43.wireOp",EDGE,"E28")])]})]});}
            extrude(context, id + "F48", {"entities" : qUnion([Q0]), "operationType" : NewBodyOperationType.ADD, "depth" : 25.4 * mm});
        }
    });
